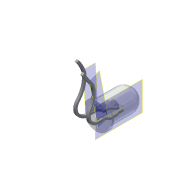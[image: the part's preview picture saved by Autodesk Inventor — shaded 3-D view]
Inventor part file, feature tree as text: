
AUTODESK INVENTOR PART (.ipt)
format: ipt  version: 2016 (Build 200138000, 138)  size: 367,616 bytes
history: native  units: mm
features: other x6, sketch x5, plane x3
ambient origin geometry x8: Origin, YZ Plane, XZ Plane, XY Plane, X Axis, Y Axis, Z Axis, Center Point
bodies: Solid1 (feature_tree), Solid2 (feature_tree)
feature tree (14):
  other  "5mm LED.ipt"
  other  "Solid1::5mm LED.ipt"
  other  "Solid2::5mm LED.ipt"
  other  "TaggingFeature1"
  sketch  "Sketch1"  dims[d0=10.0mm]
  sketch  "Sketch2"
  sketch  "Sketch4"
  sketch  "Sketch5"
  sketch  "Sketch6"
  plane  "Work Plane1"
  plane  "Work Plane2"
  plane  "Work Plane3"
  other  "Work Point1"
  other  "Work Point2"
